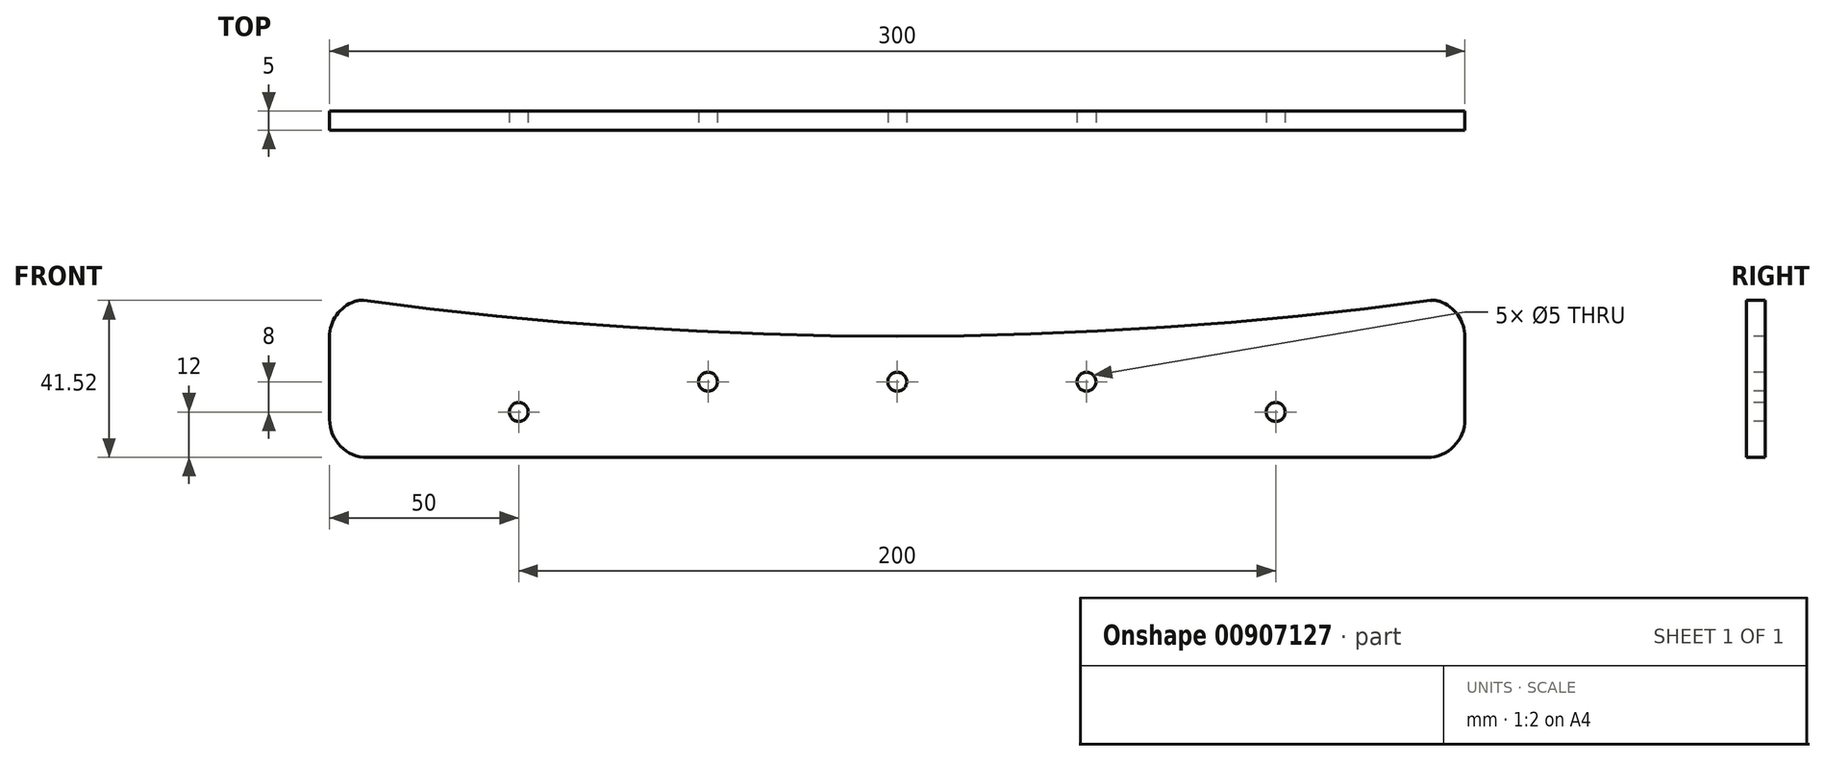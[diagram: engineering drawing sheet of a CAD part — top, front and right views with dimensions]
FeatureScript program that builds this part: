
annotation { "Feature Type Name" : "Feature", "Feature Type Description" : "" }
export const myFeature = defineFeature(function(context is Context, id is Id, definition is map)
    precondition{}
    {
        {
            var Q0;
            Q0=qCreatedBy(makeId("Front.planeOp"),FACE);
            var sketch = newSketch(context, id + "F0", { "sketchPlane" : qUnion([Q0])});
            skLineSegment(sketch, "E0", {"start": v(0, 0) * mm, "end": v(150, 0) * mm});
            skLineSegment(sketch, "E1", {"start": v(150, 0) * mm, "end": v(150, 40) * mm});
            skLineSegment(sketch, "E2", {"start": v(150, 40) * mm, "end": v(50.33, 60) * mm});
            skLineSegment(sketch, "E3", {"start": v(0, 70.22) * mm, "end": v(0, 0) * mm, "construction": true});
            skArc(sketch, "E4", {"start": v(50.33, 60) * mm, "mid": v(25.29, 63.75) * mm, "end": v(0, 65) * mm});
            skLineSegment(sketch, "E5", {"start": v(0, 65) * mm, "end": v(29, 65) * mm, "construction": true});
            skArc(sketch, "E6.MirrorCS", {"start": v(-50.33, 60) * mm, "mid": v(-25.29, 63.75) * mm, "end": v(0, 65) * mm});
            skLineSegment(sketch, "E7.MirrorCS", {"start": v(-150, 40) * mm, "end": v(-50.33, 60) * mm});
            skLineSegment(sketch, "E8.MirrorCS", {"start": v(-150, 0) * mm, "end": v(-150, 40) * mm});
            skLineSegment(sketch, "E9.MirrorCS", {"start": v(0, 0) * mm, "end": v(-150, 0) * mm});
            skSolve(sketch);
        }
        {
            var Q0;
            Q0=makeQuery(id+"F0.imprint","IMPRINT",FACE,{"disambiguationData":[TD([[makeQuery(id+"F0.imprint","IMPRINT",EDGE,{"derivedFrom":sQuery(id+"F0.wireOp",EDGE,"E0")}),1.0]])]});
            extrude(context, id + "F1", {"entities" : qUnion([Q0]), "depth" : 5 * mm, "offsetDistance" : 25 * mm});
        }
        {
            var Q0;
            Q0=makeQuery(id+"F1.opExtrude","SWEPT_EDGE",EDGE,{"disambiguationData":[OSD([sQuery(id+"F0.wireOp",EDGE,"E1"),sQuery(id+"F0.wireOp",EDGE,"E2")])]});
            var Q1;
            Q1=makeQuery(id+"F1.opExtrude","SWEPT_EDGE",EDGE,{"disambiguationData":[OSD([sQuery(id+"F0.wireOp",EDGE,"E7.MirrorCS"),sQuery(id+"F0.wireOp",EDGE,"E8.MirrorCS")])]});
            fillet(context, id + "F2", {"entities" : qUnion([Q0, Q1]), "radius" : 10 * mm, "tangentPropagation" : true, "allowEdgeOverflow" : false});
        }
        {
            var Q0;
            Q0=makeQuery(id+"F1.opExtrude","SWEPT_EDGE",EDGE,{"disambiguationData":[OSD([sQuery(id+"F0.wireOp",EDGE,"E8.MirrorCS"),sQuery(id+"F0.wireOp",EDGE,"E9.MirrorCS")])]});
            var Q1;
            Q1=makeQuery(id+"F1.opExtrude","SWEPT_EDGE",EDGE,{"disambiguationData":[OSD([sQuery(id+"F0.wireOp",EDGE,"E0"),sQuery(id+"F0.wireOp",EDGE,"E1")])]});
            fillet(context, id + "F3", {"entities" : qUnion([Q0, Q1]), "radius" : 10 * mm, "tangentPropagation" : true, "allowEdgeOverflow" : false});
        }
        {
            var Q0;
            Q0=makeQuery(id+"F1.opExtrude","CAP_FACE",FACE,{"disambiguationData":[OSD([sQuery(id+"F0.wireOp",EDGE,"E0"),sQuery(id+"F0.wireOp",EDGE,"E1"),sQuery(id+"F0.wireOp",EDGE,"E2"),sQuery(id+"F0.wireOp",EDGE,"E4"),sQuery(id+"F0.wireOp",EDGE,"E6.MirrorCS"),sQuery(id+"F0.wireOp",EDGE,"E7.MirrorCS"),sQuery(id+"F0.wireOp",EDGE,"E8.MirrorCS"),sQuery(id+"F0.wireOp",EDGE,"E9.MirrorCS")])],"isStart":false});
            var sketch = newSketch(context, id + "F4", { "sketchPlane" : qUnion([Q0])});
            skCircle(sketch, "E10", {"center": v(-50, 20) * mm, "radius": 2.5 * mm});
            skCircle(sketch, "E11", {"center": v(50, 20) * mm, "radius": 2.5 * mm});
            skCircle(sketch, "E12", {"center": v(0, 20) * mm, "radius": 2.5 * mm});
            skSolve(sketch);
        }
        {
            var Q0;
            Q0=qSketchRegion(id+"F4",true);
            extrude(context, id + "F5", {"entities" : qUnion([Q0]), "operationType" : NewBodyOperationType.REMOVE, "oppositeDirection" : true, "depth" : 25 * mm, "offsetDistance" : 25 * mm});
        }
        {
            var Q0;
            Q0=makeQuery(id+"F1.opExtrude","CAP_FACE",FACE,{"disambiguationData":[OSD([sQuery(id+"F0.wireOp",EDGE,"E0"),sQuery(id+"F0.wireOp",EDGE,"E1"),sQuery(id+"F0.wireOp",EDGE,"E2"),sQuery(id+"F0.wireOp",EDGE,"E4"),sQuery(id+"F0.wireOp",EDGE,"E6.MirrorCS"),sQuery(id+"F0.wireOp",EDGE,"E7.MirrorCS"),sQuery(id+"F0.wireOp",EDGE,"E8.MirrorCS"),sQuery(id+"F0.wireOp",EDGE,"E9.MirrorCS")])],"isStart":false});
            var sketch = newSketch(context, id + "F6", { "sketchPlane" : qUnion([Q0])});
            skCircle(sketch, "E13", {"center": v(-100, 12) * mm, "radius": 2.5 * mm});
            skLineSegment(sketch, "E14", {"start": v(-50, 20) * mm, "end": v(-50, -7.26) * mm, "construction": true});
            skCircle(sketch, "E15.MirrorC", {"center": v(100, 12) * mm, "radius": 2.5 * mm});
            skCircle(sketch, "E16.0", {"center": v(50, 20) * mm, "radius": 2.5 * mm});
            skSolve(sketch);
        }
        {
            var Q0;
            Q0=qSketchRegion(id+"F6",true);
            extrude(context, id + "F7", {"entities" : qUnion([Q0]), "operationType" : NewBodyOperationType.REMOVE, "oppositeDirection" : true, "depth" : 25 * mm, "offsetDistance" : 25 * mm});
        }
        {
            var Q0;
            Q0=makeQuery(id+"F1.opExtrude","CAP_FACE",FACE,{"disambiguationData":[OSD([sQuery(id+"F0.wireOp",EDGE,"E0"),sQuery(id+"F0.wireOp",EDGE,"E1"),sQuery(id+"F0.wireOp",EDGE,"E2"),sQuery(id+"F0.wireOp",EDGE,"E4"),sQuery(id+"F0.wireOp",EDGE,"E6.MirrorCS"),sQuery(id+"F0.wireOp",EDGE,"E7.MirrorCS"),sQuery(id+"F0.wireOp",EDGE,"E8.MirrorCS"),sQuery(id+"F0.wireOp",EDGE,"E9.MirrorCS")])],"isStart":false});
            var sketch = newSketch(context, id + "F8", { "sketchPlane" : qUnion([Q0])});
            skArc(sketch, "E17", {"start": v(-141.97, 41.61) * mm, "mid": v(0, 32.03) * mm, "end": v(141.97, 41.61) * mm});
            skLineSegment(sketch, "E18", {"start": v(-141.97, 41.61) * mm, "end": v(-141.97, 76.7) * mm});
            skLineSegment(sketch, "E19", {"start": v(-141.97, 76.7) * mm, "end": v(141.97, 76.7) * mm});
            skLineSegment(sketch, "E20", {"start": v(141.97, 76.7) * mm, "end": v(141.97, 41.61) * mm});
            skSolve(sketch);
        }
        {
            var Q0;
            Q0=makeQuery(id+"F8.imprint","IMPRINT",FACE,{"disambiguationData":[TD([[makeQuery(id+"F8.imprint","IMPRINT",EDGE,{"derivedFrom":sQuery(id+"F8.wireOp",EDGE,"E18")}),-1.0]])]});
            var Q1;
            Q1=makeQuery(id+"F8.imprint","IMPRINT",FACE,{"disambiguationData":[TD([[makeQuery(id+"F8.imprint","IMPRINT",EDGE,{"derivedFrom":sQuery(id+"F8.wireOp",EDGE,"E17")}),1.0]])]});
            extrude(context, id + "F9", {"entities" : qUnion([Q0, Q1]), "operationType" : NewBodyOperationType.REMOVE, "oppositeDirection" : true, "depth" : 25 * mm, "offsetDistance" : 25 * mm});
        }
        {
            var Q0;
            {var subQ0=sQuery(id+"F0.wireOp",EDGE,"E8.MirrorCS");var subQ1=sQuery(id+"F0.wireOp",EDGE,"E7.MirrorCS");Q0=makeQuery(id+"F9.boolean.opBoolean","MERGE",EDGE,{"derivedFrom":[makeQuery(id+"F2.opFillet","BLEND_EDGE",EDGE,{"blendedFrom":[makeQuery(id+"F1.opExtrude","SWEPT_EDGE",EDGE,{"disambiguationData":[OSD([subQ1,subQ0])]}),makeQuery(id+"F1.opExtrude","SWEPT_FACE",FACE,{"disambiguationData":[OSD([subQ1])]})],"blendedInto":[makeQuery(id+"F1.opExtrude","SWEPT_FACE",FACE,{"disambiguationData":[OSD([subQ1])]})]})],"fromTools":[makeQuery(id+"F9.opExtrude","SWEPT_EDGE",EDGE,{"disambiguationData":[OSD([sQuery(id+"F0.wireOp",EDGE,"E0"),sQuery(id+"F0.wireOp",EDGE,"E1"),sQuery(id+"F0.wireOp",EDGE,"E2"),sQuery(id+"F0.wireOp",EDGE,"E4"),sQuery(id+"F0.wireOp",EDGE,"E6.MirrorCS"),subQ1,subQ0,sQuery(id+"F0.wireOp",EDGE,"E9.MirrorCS"),sQuery(id+"F8.wireOp",EDGE,"E17"),sQuery(id+"F8.wireOp",EDGE,"E18")])]})]});}
            var Q1;
            {var subQ0=sQuery(id+"F0.wireOp",EDGE,"E2");var subQ1=sQuery(id+"F0.wireOp",EDGE,"E1");Q1=makeQuery(id+"F9.boolean.opBoolean","MERGE",EDGE,{"derivedFrom":[makeQuery(id+"F2.opFillet","BLEND_EDGE",EDGE,{"blendedFrom":[makeQuery(id+"F1.opExtrude","SWEPT_EDGE",EDGE,{"disambiguationData":[OSD([subQ1,subQ0])]}),makeQuery(id+"F1.opExtrude","SWEPT_FACE",FACE,{"disambiguationData":[OSD([subQ0])]})],"blendedInto":[makeQuery(id+"F1.opExtrude","SWEPT_FACE",FACE,{"disambiguationData":[OSD([subQ0])]})]})],"fromTools":[makeQuery(id+"F9.opExtrude","SWEPT_EDGE",EDGE,{"disambiguationData":[OSD([sQuery(id+"F0.wireOp",EDGE,"E0"),subQ1,subQ0,sQuery(id+"F0.wireOp",EDGE,"E4"),sQuery(id+"F0.wireOp",EDGE,"E6.MirrorCS"),sQuery(id+"F0.wireOp",EDGE,"E7.MirrorCS"),sQuery(id+"F0.wireOp",EDGE,"E8.MirrorCS"),sQuery(id+"F0.wireOp",EDGE,"E9.MirrorCS"),sQuery(id+"F8.wireOp",EDGE,"E17"),sQuery(id+"F8.wireOp",EDGE,"E20")])]})]});}
            fillet(context, id + "F10", {"entities" : qUnion([Q0, Q1]), "radius" : 5 * mm, "tangentPropagation" : true, "allowEdgeOverflow" : false});
        }
    });
